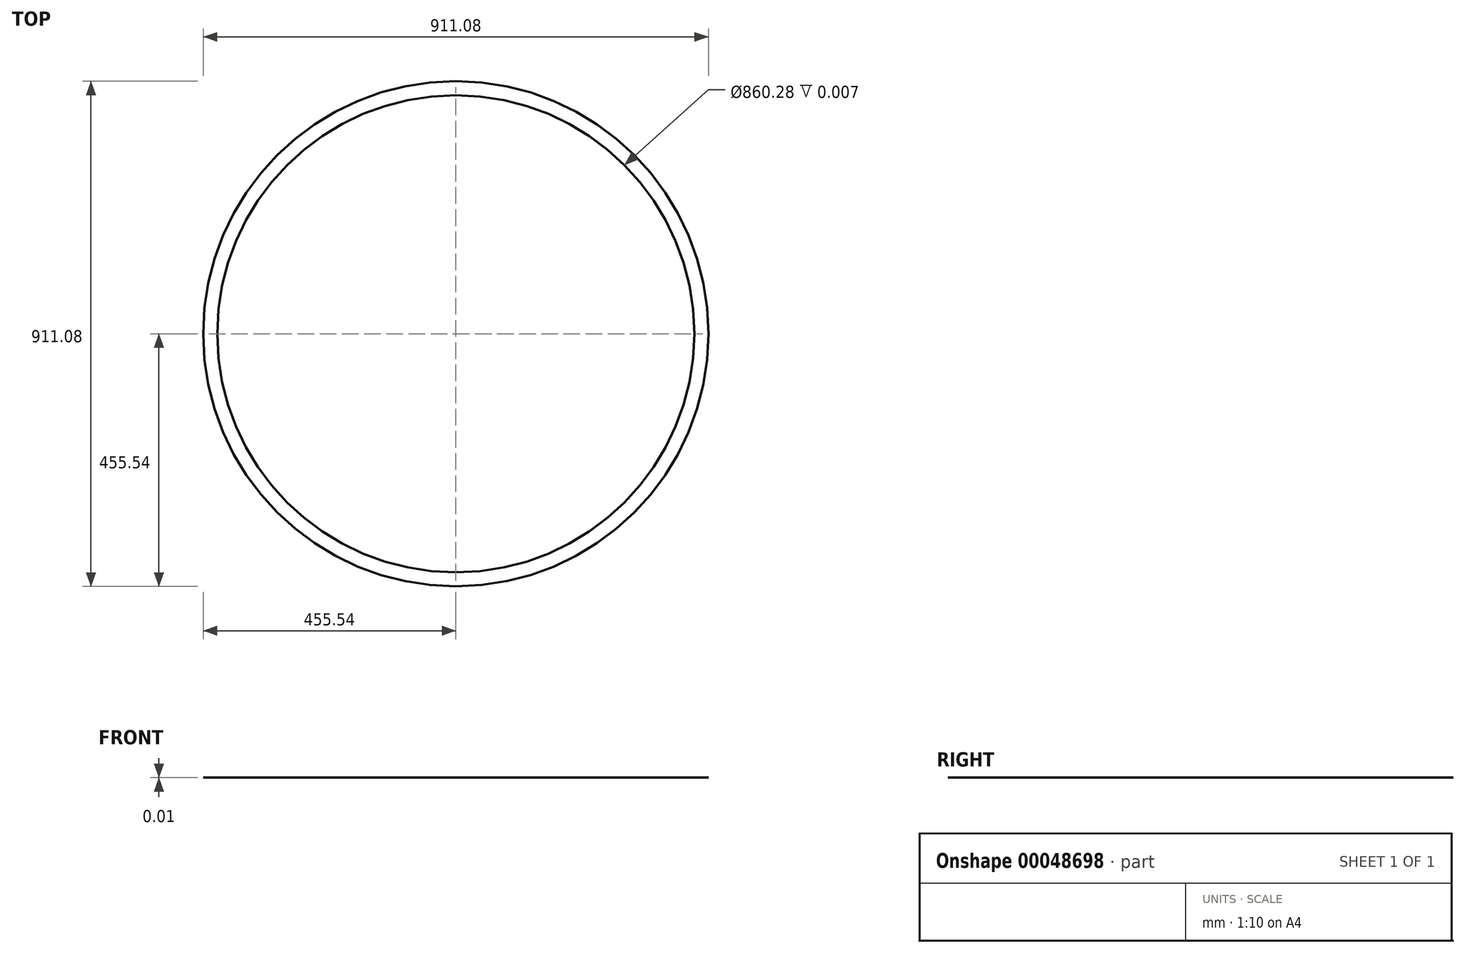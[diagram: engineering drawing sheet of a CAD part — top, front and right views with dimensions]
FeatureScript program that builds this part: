
annotation { "Feature Type Name" : "Feature", "Feature Type Description" : "" }
export const myFeature = defineFeature(function(context is Context, id is Id, definition is map)
    precondition{}
    {
        {
            var Q0;
            Q0=qCreatedBy(makeId("Top.planeOp"),FACE);
            var sketch = newSketch(context, id + "F0", { "sketchPlane" : qUnion([Q0])});
            skCircle(sketch, "E0", {"center": v(0, 0) * mm, "radius": 455.54 * mm});
            skCircle(sketch, "E1", {"center": v(0, 0) * mm, "radius": 430.14 * mm});
            skSolve(sketch);
        }
        {
            var Q0;
            Q0 = qSketchRegion(id + "F0", true);
            extrude(context, id + "F1", {"entities" : qUnion([Q0]), "depth" : 3 / 457.2 * mm});
        }
    });
